# Revit family: NLRS_57_AIR_UN_perforated-ceiling-diffuser-crvmiob_LT_sacs
name_source: partatom
category: Air Terminals
units: mm (PartAtom-declared; Revit-internal decimal feet)

## family parameters
Always vertical = Yes
Cut with Voids When Loaded = No
Part Type = Normal
Room Calculation Point = Yes
Round Connector Dimension = Use Diameter
Shared = No
Work Plane-Based = No

## types (4) — shared parameters
Assembly Code = 57
Default Elevation = 2700 mm  [stored 8.85827 ft]
Description = Perforated return clean-grill for use in modulair ceilings, Type CRVMI
Flip_Connector_to_left = No
IfcDescription = Perforated return clean-grill for use in modulair ceilings, Type CRVMI
IfcExportAs = IfcAirterminal
IfcExportType = Diffuser
Manufacturer = Solid Air Climate Solutions
Model = CRVMI
NLRS_C_content_datum_uitgifte = 30-07-2025
NLRS_C_content_provider = Solid Air Climate Solutions
NLRS_C_content_versie = 4.22.02
NLRS_C_description = Perforated return clean-grill for use in modulair ceilings, Type CRVMI
SACS_Data_Hidden = CRVMIOB
SACS_Data_Hidden2 = Grill_Selection_Factors
URL = https://solid-air.nl
zero-valued in all types: Cost

## per-type parameters (varying)
| type | Max Flow | Min Flow | SACS_Base_Index |
| 450 | 540.0 m³/h | 252.0 m³/h | 4 |
| 200 | 144.0 m³/h | 54.0 m³/h | 1 |
| 250 | 215.0 m³/h | 90.0 m³/h | 2 |
| 350 | 360.0 m³/h | 144.0 m³/h | 3 |

note: [stored X ft] marks values corroborated as IEEE doubles in the binary element streams (Revit-internal decimal feet)

## geometry (parser evidence)
native form markers: Sweep x17
no freeform markers — native parametric forms only
